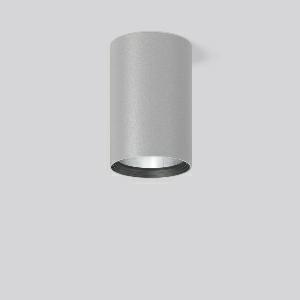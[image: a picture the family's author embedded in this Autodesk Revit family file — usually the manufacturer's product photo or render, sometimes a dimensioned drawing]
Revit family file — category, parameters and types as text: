
# Revit family: heledon_maxi_a_931223_004_1_76_0b70
name_source: partatom
category: Lighting Fixtures
units: mm (PartAtom-declared; Revit-internal decimal feet)

## family parameters
Cut with Voids When Loaded = No
Host = Face
Light Source = No
Part Type = Normal
Room Calculation Point = No
Round Connector Dimension = Use Diameter
Shared = No

## types (1)
- HELEDON maxi A (1 x LED Modul 940, 4400 lm, 4000)
    Apparent Load = 35 VA
    Approval mark = CE
    CIE Flux Codes = 100 100 100 100 100
    Color Rendering = 92
    Color Temperature = 4000
    Default Elevation = 1800 mm
    Description = Series: HELEDON maxi
Cylindrical surface-mounted downlight. Housing: die-cast aluminium, powder-coated. Internal ceiling frame polycarbonate with bayonet mounting. Black plastic ring and recessed LED to prevent glare from the side. Optical assembly with reflector made of MIRO-Silver with 98% total light reflection for outstanding efficiency - can be changed without tools. Best colour rendering index Ra>90. Suitable for Ceiling mounting. Easy installation with a separate ceiling frame with bayonet mounting and plug connection. Driver integrated. Connected via plug-in connector. High quality converter without flickering and stroboscopic effect. The following accessories can be mounted without use of tools: interchangeable lenses, decorative glasses, honeycomb louvre, clear and frosted diffusers, white interchangeable plastic ring. 
Colour: silver
Diameter: 123 mm
Height: 183 mm
Lamp: LED
Socket: without socket
Colour temperature: 4000K
Colour rendering index (CRI): 92
System power: 35 W
Rated luminous flux: 4400 lm
Luminous efficiency: 126 lm/W
Control gear: Converter, dimmable, DALI
Protection class: I
Type of protection: IP 20
    Height = 183 mm
    Lamp = 1 x LED Modul 940
    Lamp Light Flux = 4400 lm
    Lamp count = 1
    Length = 123 mm
    Lifetime = 50000 h
    Luminous efficacy = 126 lm/W
    Manufacturer = RZB
    ModVariant = No
    Model = 931223.004.1.76
    Mounting Place = Ceiling
    Mounting Type = Surface mounted
    Number of Poles = 1
    OnlyDefault = Yes
    Power Factor = 1
    Product Name = HELEDON maxi A
    Product group = Surface mounted downlights
    ProductGroupID = 302
    Protection Class = Protection class I
    Protection Degree = IP 20
    RLX_Detail_Level = 1
    RLX_Emergency_Light_Flux = 0 lm
    RLX_Emergency_Type = 0
    RLX_Emergency_Type_DB = No
    RlxData = <blob elided: 97921 chars, md5=84985b87>
    Socket = socket
    Standby Power = 0 W
    System Light Flux = 4400 lm
    System Power = 35 W
    Type Comments = Product without accessories
    Type Image = 931192.004.jpg
    URL = http://relux.com
    VarID = ---
    Voltage = 230 V
    Voltage Range = 220-240 V
    Weight = 0.00 kg
    Width = 0 mm  [stored 0 ft]

note: [stored X ft] marks values corroborated as IEEE doubles in the binary element streams (Revit-internal decimal feet)

## geometry (parser evidence)
native form markers: Blend x4, Sweep x9
no freeform markers — native parametric forms only
